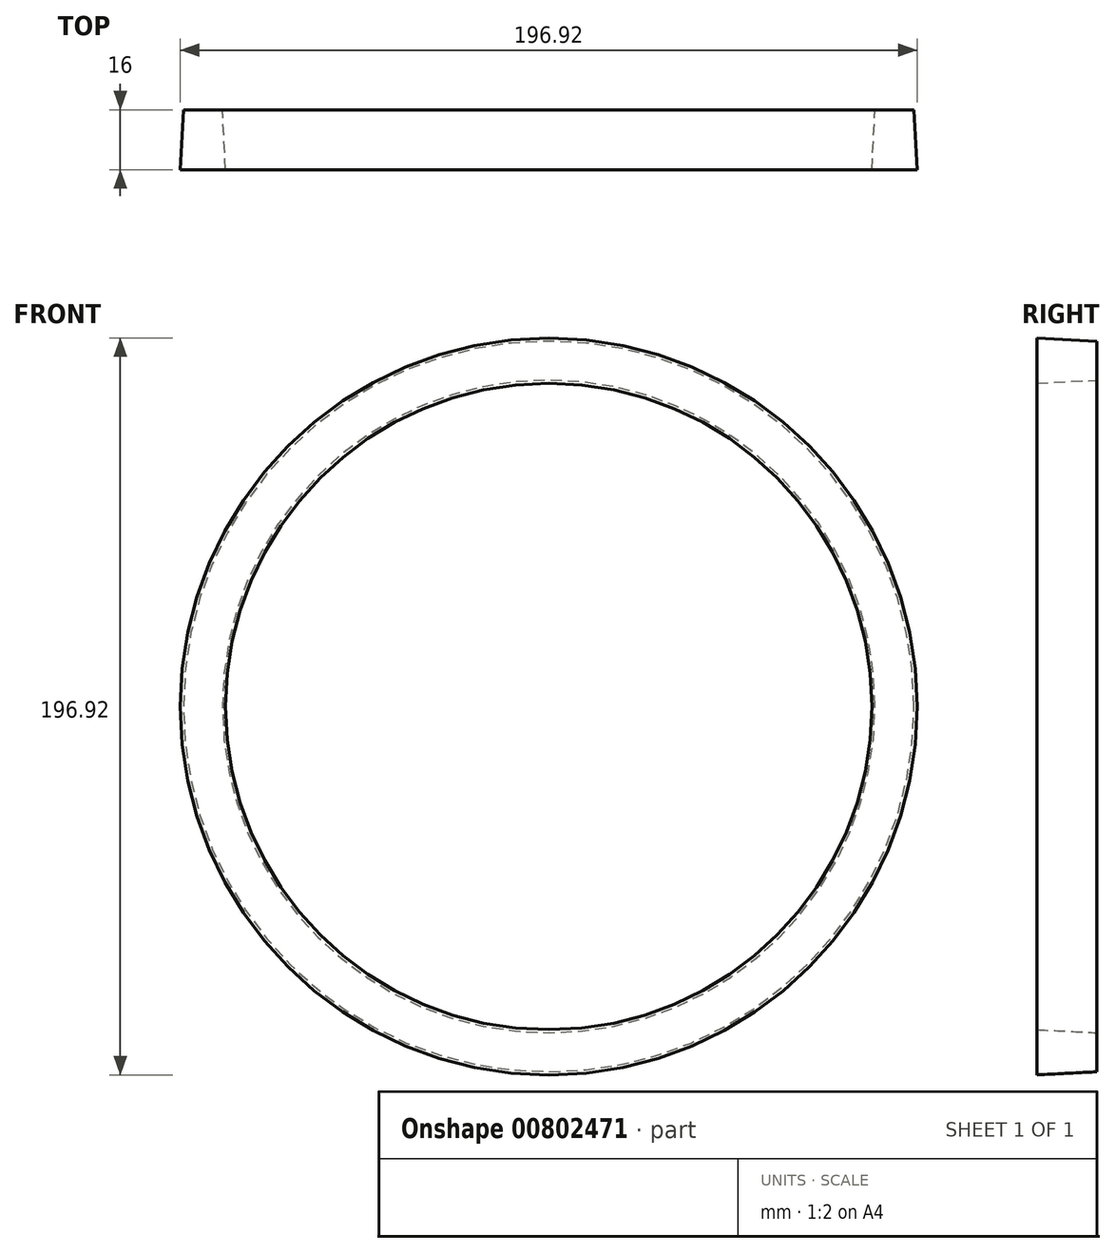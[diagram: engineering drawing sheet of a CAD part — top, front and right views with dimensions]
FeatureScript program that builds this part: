
annotation { "Feature Type Name" : "Feature", "Feature Type Description" : "" }
export const myFeature = defineFeature(function(context is Context, id is Id, definition is map)
    precondition{}
    {
        {
            var Q0;
            Q0=qCreatedBy(makeId("Front.planeOp"),FACE);
            var sketch = newSketch(context, id + "F0", { "sketchPlane" : qUnion([Q0])});
            skCircle(sketch, "E0", {"center": v(0, 0) * mm, "radius": 97.62 * mm});
            skCircle(sketch, "E1.0", {"center": v(0, 0) * mm, "radius": 87.2 * mm});
            skSolve(sketch);
        }
        {
            var Q0;
            Q0=makeQuery(id+"F0.imprint","IMPRINT",FACE,{"disambiguationData":[TD([[makeQuery(id+"F0.imprint","IMPRINT",EDGE,{"derivedFrom":sQuery(id+"F0.wireOp",EDGE,"E0")}),1.0]])]});
            extrude(context, id + "F1", {"entities" : qUnion([Q0]), "depth" : 16 * mm, "offsetDistance" : 25.4 * mm, "hasDraft" : true, "draftAngle" : 3 * degree});
        }
    });
